# Revit family: P191568KX-100c_KXU2830Y
name_source: partatom
category: Specialty Equipment
units: mm (PartAtom-declared; Revit-internal decimal feet)

## family parameters
Always vertical = Yes
Cut with Voids When Loaded = No
Enable Cutting in Views = No
Maintain Annotation Orientation = No
Part Type = Normal
Room Calculation Point = No
Round Connector Dimension = Use Diameter
Shared = No
Work Plane-Based = No

## types (1)
- KXU2830YSS
    Accent Material = ARCAT - Metal - Steel - Stainless
    Amps = 15 A
    Body Material = ARCAT - Metal - Steel - Stainless
    Default Elevation = 0"
    Depth = 18 7/8"
    Description = 30'' Slide-Out 400 CFM
Hotte rétractable de 30 po, 400 pi cu/min
    Dimension Guide = http://access.whirlpool.com Guide&sku=KXU2830YSS&language=EN
http://access.whirlpool.com Guide&sku=KXU2830YSS&language=EN
    Family Name = COOKING
    Feature 1 = 65K BTU Threshold
Seuil de 65 000 BTU
    Feature 2 = Flush to Cabinetry
Affleurant au placard
    Feature 3 = 4-Speed Electronic Touch Control with LED Display
Commande électronique à 4 vitesses avec affichage ACL
    Height = 12 9/16"
    Installation-Fabrication = http://access.whirlpool.com Instruction&sku=KXU2830YSS&language=EN
http://access.whirlpool.com Instruction&sku=KXU2830YSS&language=FR
    Knob Material = ARCAT - Metal - Steel - Black
    Manufacturer = Jenn Air
    Model = KXU2830YSS
    Voltage = 0 V
    Width = 30"
